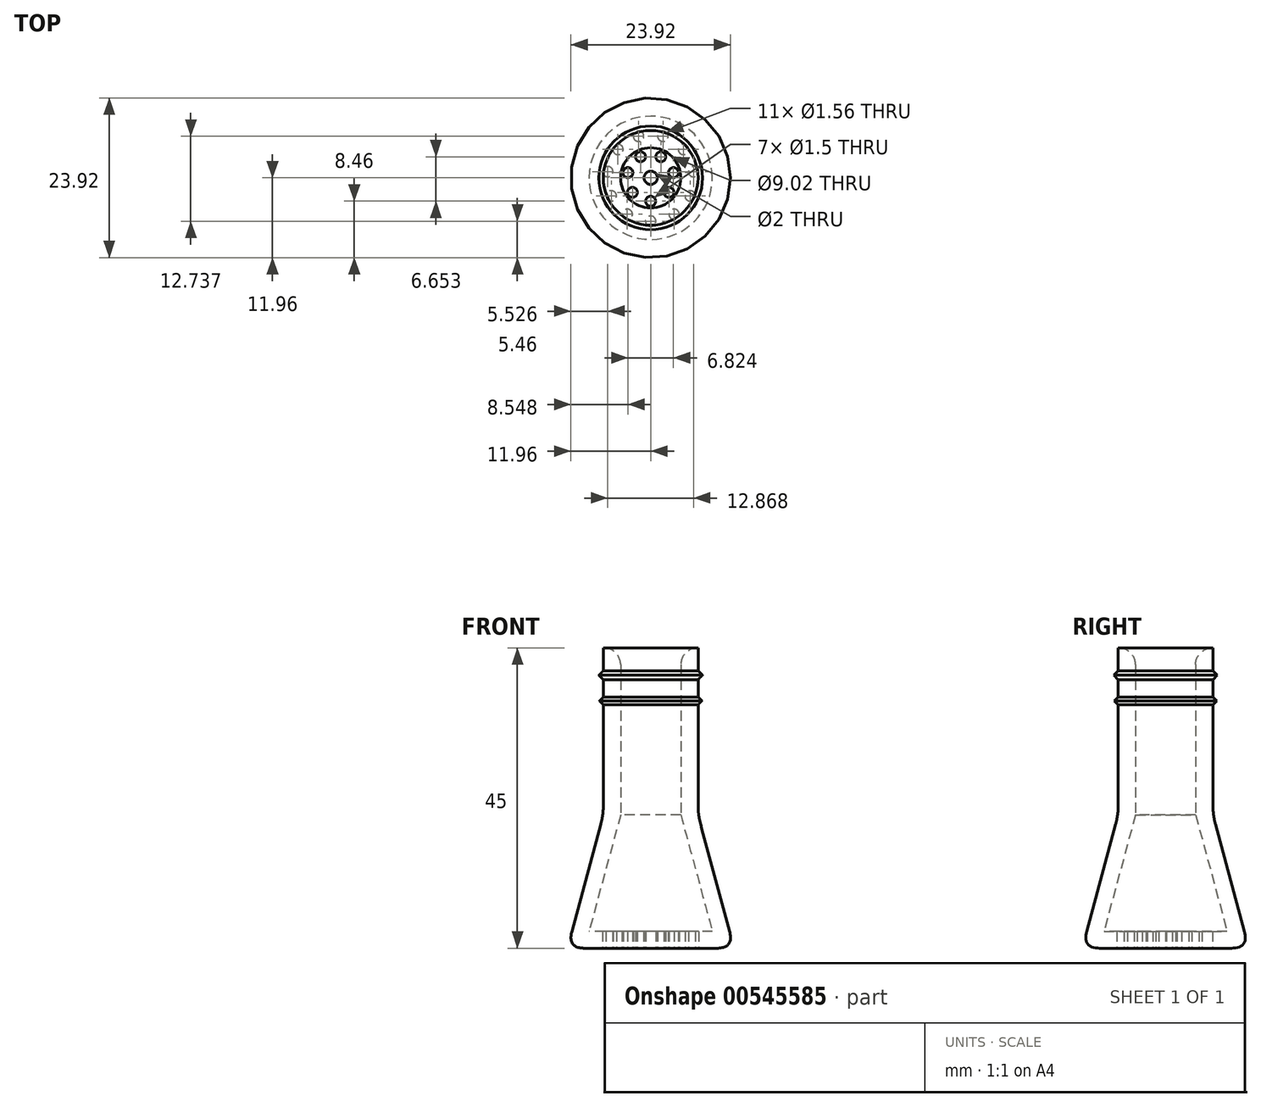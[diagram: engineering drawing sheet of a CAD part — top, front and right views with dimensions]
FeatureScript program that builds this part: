
annotation { "Feature Type Name" : "Feature", "Feature Type Description" : "" }
export const myFeature = defineFeature(function(context is Context, id is Id, definition is map)
    precondition{}
    {
        {
            var Q0;
            Q0=qCreatedBy(makeId("Top.planeOp"),FACE);
            var sketch = newSketch(context, id + "F0", { "sketchPlane" : qUnion([Q0])});
            skCircle(sketch, "E0", {"center": v(0, 0) * mm, "radius": 12.5 * mm});
            skSolve(sketch);
        }
        {
            var Q0;
            Q0=qCreatedBy(makeId("Top.planeOp"),FACE);
            cPlane(context, id + "F1", {"entities" : qUnion([Q0]), "cplaneType" : CPlaneType.OFFSET, "offset" : 20 * mm, "width" : 150 * mm, "height" : 150 * mm});
        }
        {
            var Q0;
            Q0=qCreatedBy(id+"F1.planeOp",FACE);
            var sketch = newSketch(context, id + "F2", { "sketchPlane" : qUnion([Q0])});
            skCircle(sketch, "E1", {"center": v(0, 0) * mm, "radius": 7.1 * mm});
            skSolve(sketch);
        }
        {
            var Q0;
            Q0=makeQuery(id+"F0.imprint","IMPRINT",FACE,{"disambiguationData":[TD([[makeQuery(id+"F0.imprint","IMPRINT",EDGE,{"derivedFrom":sQuery(id+"F0.wireOp",EDGE,"E0")}),1.0]])]});
            var Q1;
            Q1=makeQuery(id+"F2.imprint","IMPRINT",FACE,{"disambiguationData":[TD([[makeQuery(id+"F2.imprint","IMPRINT",EDGE,{"derivedFrom":sQuery(id+"F2.wireOp",EDGE,"E1")}),1.0]])]});
            loft(context, id + "F3", {"sheetProfilesArray" : [{ "sheetProfileEntities" : qUnion([Q0]) }, { "sheetProfileEntities" : qUnion([Q1]) }]});
        }
        {
            var Q0;
            Q0=makeQuery(id+"F3.opLoft","CAP_FACE",FACE,{"disambiguationData":[OSD([makeQuery(id+"F2.imprint","IMPRINT",FACE,{"disambiguationData":[TD([[makeQuery(id+"F2.imprint","IMPRINT",EDGE,{"derivedFrom":sQuery(id+"F2.wireOp",EDGE,"E1")}),1.0]])]})])],"isStart":true});
            var Q1;
            Q1=makeQuery(id+"F5.opExtrude","SWEPT_FACE",FACE,{"disambiguationData":[OSD([sQuery(id+"F0.wireOp",EDGE,"E0"),sQuery(id+"F2.wireOp",EDGE,"E1")])]});
            var Q2;
            Q2=makeQuery(id+"F3.opLoft","SWEPT_BODY",BODY,{"disambiguationData":[OSD([makeQuery(id+"F0.imprint","IMPRINT",FACE,{"disambiguationData":[TD([[makeQuery(id+"F0.imprint","IMPRINT",EDGE,{"derivedFrom":sQuery(id+"F0.wireOp",EDGE,"E0")}),1.0]])]}),makeQuery(id+"F2.imprint","IMPRINT",FACE,{"disambiguationData":[TD([[makeQuery(id+"F2.imprint","IMPRINT",EDGE,{"derivedFrom":sQuery(id+"F2.wireOp",EDGE,"E1")}),1.0]])]})])]});
            shell(context, id + "F4", {"entities" : qUnion([Q0, Q1]), "parts" : qUnion([Q2]), "thickness" : 2.5 * mm});
        }
        {
            var Q0;
            Q0=makeQuery(id+"F0ecNTMsgWaadGP_1.imprint","IMPRINT",FACE,{"disambiguationData":[TD([[makeQuery(id+"F0ecNTMsgWaadGP_1.imprint","IMPRINT",EDGE,{"derivedFrom":sQuery(id+"F0ecNTMsgWaadGP_1.wireOp",EDGE,"DrDFBUXE-mWmM-yVQ1-YrQf-KKvgjwECMo2q")}),1.0]])]});
            var Q1;
            Q1=makeQuery(id+"F3.opLoft","CAP_FACE",FACE,{"disambiguationData":[OSD([makeQuery(id+"F2.imprint","IMPRINT",FACE,{"disambiguationData":[TD([[makeQuery(id+"F2.imprint","IMPRINT",EDGE,{"derivedFrom":sQuery(id+"F2.wireOp",EDGE,"E1")}),1.0]])]})])],"isStart":true});
            extrude(context, id + "F5", {"entities" : qUnion([Q0, Q1]), "operationType" : NewBodyOperationType.ADD, "depth" : 25 * mm, "offsetDistance" : 25 * mm});
        }
        {
            var Q0;
            Q0=makeQuery(id+"F3.opLoft","CAP_FACE",FACE,{"disambiguationData":[OSD([makeQuery(id+"F0.imprint","IMPRINT",FACE,{"disambiguationData":[TD([[makeQuery(id+"F0.imprint","IMPRINT",EDGE,{"derivedFrom":sQuery(id+"F0.wireOp",EDGE,"E0")}),1.0]])]})])],"isStart":true});
            var sketch = newSketch(context, id + "F6", { "sketchPlane" : qUnion([Q0])});
            skCircle(sketch, "E2", {"center": v(0, 0) * mm, "radius": 1 * mm});
            skCircle(sketch, "E3", {"center": v(0, 3.5) * mm, "radius": 0.75 * mm});
            skCircle(sketch, "E4.1.0", {"center": v(-2.74, 2.18) * mm, "radius": 0.75 * mm});
            skCircle(sketch, "E4.2.0", {"center": v(-3.41, -0.78) * mm, "radius": 0.75 * mm});
            skCircle(sketch, "E4.3.0", {"center": v(-1.52, -3.15) * mm, "radius": 0.75 * mm});
            skCircle(sketch, "E4.4.0", {"center": v(1.52, -3.15) * mm, "radius": 0.75 * mm});
            skCircle(sketch, "E5.1.5.0", {"center": v(3.41, -0.78) * mm, "radius": 0.75 * mm});
            skCircle(sketch, "E5.1.6.0", {"center": v(2.74, 2.18) * mm, "radius": 0.75 * mm});
            skCircle(sketch, "E6", {"center": v(0, 6.5) * mm, "radius": 0.78 * mm});
            skCircle(sketch, "E7.1.0", {"center": v(-3.51, 5.47) * mm, "radius": 0.78 * mm});
            skCircle(sketch, "E7.2.0", {"center": v(-5.91, 2.7) * mm, "radius": 0.78 * mm});
            skCircle(sketch, "E7.3.0", {"center": v(-6.43, -0.93) * mm, "radius": 0.78 * mm});
            skCircle(sketch, "E7.4.0", {"center": v(-4.91, -4.26) * mm, "radius": 0.78 * mm});
            skCircle(sketch, "E7.5.0", {"center": v(-1.83, -6.24) * mm, "radius": 0.78 * mm});
            skCircle(sketch, "E7.6.0", {"center": v(1.83, -6.24) * mm, "radius": 0.78 * mm});
            skCircle(sketch, "E7.7.0", {"center": v(4.91, -4.26) * mm, "radius": 0.78 * mm});
            skCircle(sketch, "E7.8.0", {"center": v(6.43, -0.93) * mm, "radius": 0.78 * mm});
            skCircle(sketch, "E7.9.0", {"center": v(5.91, 2.7) * mm, "radius": 0.78 * mm});
            skCircle(sketch, "E8.0.10.0", {"center": v(3.51, 5.47) * mm, "radius": 0.78 * mm});
            skSolve(sketch);
        }
        {
            var Q0;
            Q0=makeQuery(id+"F3.opLoft","MID_CAP_EDGE",EDGE,{"disambiguationData":[OSD([sQuery(id+"F0.wireOp",EDGE,"E0")])],"capPos":0.0});
            fillet(context, id + "F7", {"entities" : qUnion([Q0]), "radius" : 2 * mm, "tangentPropagation" : true, "rho" : .5, "crossSection" : FilletCrossSection.CONIC, "allowEdgeOverflow" : false});
        }
        {
            var Q0;
            Q0=makeQuery(id+"F6.imprint","IMPRINT",FACE,{"disambiguationData":[TD([[makeQuery(id+"F6.imprint","IMPRINT",EDGE,{"derivedFrom":sQuery(id+"F6.wireOp",EDGE,"E4.1.0")}),1.0]])]});
            var Q1;
            Q1=makeQuery(id+"F6.imprint","IMPRINT",FACE,{"disambiguationData":[TD([[makeQuery(id+"F6.imprint","IMPRINT",EDGE,{"derivedFrom":sQuery(id+"F6.wireOp",EDGE,"E4.2.0")}),1.0]])]});
            var Q2;
            Q2=makeQuery(id+"F6.imprint","IMPRINT",FACE,{"disambiguationData":[TD([[makeQuery(id+"F6.imprint","IMPRINT",EDGE,{"derivedFrom":sQuery(id+"F6.wireOp",EDGE,"E2")}),1.0]])]});
            var Q3;
            Q3=makeQuery(id+"F6.imprint","IMPRINT",FACE,{"disambiguationData":[TD([[makeQuery(id+"F6.imprint","IMPRINT",EDGE,{"derivedFrom":sQuery(id+"F6.wireOp",EDGE,"E4.3.0")}),1.0]])]});
            var Q4;
            Q4=makeQuery(id+"F6.imprint","IMPRINT",FACE,{"disambiguationData":[TD([[makeQuery(id+"F6.imprint","IMPRINT",EDGE,{"derivedFrom":sQuery(id+"F6.wireOp",EDGE,"E4.4.0")}),1.0]])]});
            var Q5;
            Q5=makeQuery(id+"F6.imprint","IMPRINT",FACE,{"disambiguationData":[TD([[makeQuery(id+"F6.imprint","IMPRINT",EDGE,{"derivedFrom":sQuery(id+"F6.wireOp",EDGE,"E3")}),1.0]])]});
            var Q6;
            Q6=makeQuery(id+"F6.imprint","IMPRINT",FACE,{"disambiguationData":[TD([[makeQuery(id+"F6.imprint","IMPRINT",EDGE,{"derivedFrom":sQuery(id+"F6.wireOp",EDGE,"E5.1.6.0")}),1.0]])]});
            var Q7;
            Q7=makeQuery(id+"F6.imprint","IMPRINT",FACE,{"disambiguationData":[TD([[makeQuery(id+"F6.imprint","IMPRINT",EDGE,{"derivedFrom":sQuery(id+"F6.wireOp",EDGE,"E5.1.5.0")}),1.0]])]});
            var Q8;
            Q8=makeQuery(id+"F6.imprint","IMPRINT",FACE,{"disambiguationData":[TD([[makeQuery(id+"F6.imprint","IMPRINT",EDGE,{"derivedFrom":sQuery(id+"F6.wireOp",EDGE,"E8.0.10.0")}),1.0]])]});
            var Q9;
            Q9=makeQuery(id+"F6.imprint","IMPRINT",FACE,{"disambiguationData":[TD([[makeQuery(id+"F6.imprint","IMPRINT",EDGE,{"derivedFrom":sQuery(id+"F6.wireOp",EDGE,"E7.9.0")}),1.0]])]});
            var Q10;
            Q10=makeQuery(id+"F6.imprint","IMPRINT",FACE,{"disambiguationData":[TD([[makeQuery(id+"F6.imprint","IMPRINT",EDGE,{"derivedFrom":sQuery(id+"F6.wireOp",EDGE,"E7.8.0")}),1.0]])]});
            var Q11;
            Q11=makeQuery(id+"F6.imprint","IMPRINT",FACE,{"disambiguationData":[TD([[makeQuery(id+"F6.imprint","IMPRINT",EDGE,{"derivedFrom":sQuery(id+"F6.wireOp",EDGE,"E7.7.0")}),1.0]])]});
            var Q12;
            Q12=makeQuery(id+"F6.imprint","IMPRINT",FACE,{"disambiguationData":[TD([[makeQuery(id+"F6.imprint","IMPRINT",EDGE,{"derivedFrom":sQuery(id+"F6.wireOp",EDGE,"E7.6.0")}),1.0]])]});
            var Q13;
            Q13=makeQuery(id+"F6.imprint","IMPRINT",FACE,{"disambiguationData":[TD([[makeQuery(id+"F6.imprint","IMPRINT",EDGE,{"derivedFrom":sQuery(id+"F6.wireOp",EDGE,"E7.5.0")}),1.0]])]});
            var Q14;
            Q14=makeQuery(id+"F6.imprint","IMPRINT",FACE,{"disambiguationData":[TD([[makeQuery(id+"F6.imprint","IMPRINT",EDGE,{"derivedFrom":sQuery(id+"F6.wireOp",EDGE,"E7.4.0")}),1.0]])]});
            var Q15;
            Q15=makeQuery(id+"F6.imprint","IMPRINT",FACE,{"disambiguationData":[TD([[makeQuery(id+"F6.imprint","IMPRINT",EDGE,{"derivedFrom":sQuery(id+"F6.wireOp",EDGE,"E7.3.0")}),1.0]])]});
            var Q16;
            Q16=makeQuery(id+"F6.imprint","IMPRINT",FACE,{"disambiguationData":[TD([[makeQuery(id+"F6.imprint","IMPRINT",EDGE,{"derivedFrom":sQuery(id+"F6.wireOp",EDGE,"E7.2.0")}),1.0]])]});
            var Q17;
            Q17=makeQuery(id+"F6.imprint","IMPRINT",FACE,{"disambiguationData":[TD([[makeQuery(id+"F6.imprint","IMPRINT",EDGE,{"derivedFrom":sQuery(id+"F6.wireOp",EDGE,"E7.1.0")}),1.0]])]});
            var Q18;
            Q18=makeQuery(id+"F6.imprint","IMPRINT",FACE,{"disambiguationData":[TD([[makeQuery(id+"F6.imprint","IMPRINT",EDGE,{"derivedFrom":sQuery(id+"F6.wireOp",EDGE,"E6")}),1.0]])]});
            var Q19;
            Q19=makeQuery(id+"F3.opLoft","CAP_FACE",FACE,{"disambiguationData":[OSD([makeQuery(id+"F2.imprint","IMPRINT",FACE,{"disambiguationData":[TD([[makeQuery(id+"F2.imprint","IMPRINT",EDGE,{"derivedFrom":sQuery(id+"F2.wireOp",EDGE,"E1")}),1.0]])]})])],"isStart":true});
            extrude(context, id + "F8", {"entities" : qUnion([Q0, Q1, Q2, Q3, Q4, Q5, Q6, Q7, Q8, Q9, Q10, Q11, Q12, Q13, Q14, Q15, Q16, Q17, Q18]), "operationType" : NewBodyOperationType.REMOVE, "oppositeDirection" : true, "depth" : 3 * mm, "endBoundEntityFace" : qUnion([Q19]), "offsetDistance" : 25 * mm});
        }
        {
            var Q0;
            {var subQ0=sQuery(id+"F2.wireOp",EDGE,"E1");var subQ1=sQuery(id+"F0.wireOp",EDGE,"E0");var subQ2=makeQuery(id+"F3.opLoft","MID_CAP_EDGE",EDGE,{"disambiguationData":[OSD([subQ1,subQ0])],"capPos":1.0});Q0=makeQuery(id+"F5.boolean.opBoolean","MERGE",EDGE,{"derivedFrom":[subQ2,makeQuery(id+"F5.opExtrude","CAP_EDGE",EDGE,{"disambiguationData":[OSD([subQ1,subQ0]),TDD([subQ2])],"isStart":true})]});}
            fillet(context, id + "F9", {"entities" : qUnion([Q0]), "radius" : 11 * mm, "tangentPropagation" : true, "allowEdgeOverflow" : false});
        }
        {
            var Q0;
            Q0=qCreatedBy(makeId("Front.planeOp"),FACE);
            var sketch = newSketch(context, id + "F10", { "sketchPlane" : qUnion([Q0])});
            skLineSegment(sketch, "E9.bottom", {"start": v(6.68, 36.07) * mm, "end": v(7.68, 36.07) * mm});
            skLineSegment(sketch, "E9.top", {"start": v(6.68, 38.07) * mm, "end": v(7.68, 38.07) * mm});
            skLineSegment(sketch, "E9.left", {"start": v(6.68, 36.07) * mm, "end": v(6.68, 38.07) * mm});
            skLineSegment(sketch, "E9.right", {"start": v(7.68, 36.07) * mm, "end": v(7.68, 38.07) * mm});
            skLineSegment(sketch, "E10.bottom", {"start": v(6.77, 39.92) * mm, "end": v(7.77, 39.92) * mm});
            skLineSegment(sketch, "E10.top", {"start": v(6.77, 41.92) * mm, "end": v(7.77, 41.92) * mm});
            skLineSegment(sketch, "E10.left", {"start": v(6.77, 39.92) * mm, "end": v(6.77, 41.92) * mm});
            skLineSegment(sketch, "E10.right", {"start": v(7.77, 39.92) * mm, "end": v(7.77, 41.92) * mm});
            skSolve(sketch);
        }
        {
            var Q0;
            Q0=makeQuery(id+"F10.imprint","IMPRINT",FACE,{"disambiguationData":[TD([[makeQuery(id+"F10.imprint","IMPRINT",EDGE,{"derivedFrom":sQuery(id+"F10.wireOp",EDGE,"E9.bottom")}),1.0]])]});
            var Q1;
            Q1=makeQuery(id+"F10.imprint","IMPRINT",FACE,{"disambiguationData":[TD([[makeQuery(id+"F10.imprint","IMPRINT",EDGE,{"derivedFrom":sQuery(id+"F10.wireOp",EDGE,"E10.bottom")}),1.0]])]});
            var Q2;
            {var subQ0=sQuery(id+"F2.wireOp",EDGE,"E1");var subQ1=sQuery(id+"F0.wireOp",EDGE,"E0");Q2=makeQuery(id+"F5.opExtrude","SWEPT_FACE",FACE,{"disambiguationData":[OSD([subQ1,subQ0]),TDD([makeQuery(id+"F3.opLoft","MID_CAP_EDGE",EDGE,{"disambiguationData":[OSD([subQ1,subQ0])],"capPos":1.0})])]});}
            revolve(context, id + "F11", {"operationType" : NewBodyOperationType.ADD, "entities" : qUnion([Q0, Q1]), "axis" : qUnion([Q2]), "revolveType" : RevolveType.FULL});
        }
        {
            var Q0;
            Q0=makeQuery(id+"F11.opRevolve","SWEPT_EDGE",EDGE,{"disambiguationData":[OSD([sQuery(id+"F10.wireOp",EDGE,"E9.top"),sQuery(id+"F10.wireOp",EDGE,"E9.right")])]});
            var Q1;
            Q1=makeQuery(id+"F11.opRevolve","SWEPT_EDGE",EDGE,{"disambiguationData":[OSD([sQuery(id+"F10.wireOp",EDGE,"E9.bottom"),sQuery(id+"F10.wireOp",EDGE,"E9.right")])]});
            var Q2;
            Q2=makeQuery(id+"F11.opRevolve","SWEPT_EDGE",EDGE,{"disambiguationData":[OSD([sQuery(id+"F10.wireOp",EDGE,"E10.bottom"),sQuery(id+"F10.wireOp",EDGE,"E10.right")])]});
            var Q3;
            Q3=makeQuery(id+"F11.opRevolve","SWEPT_EDGE",EDGE,{"disambiguationData":[OSD([sQuery(id+"F10.wireOp",EDGE,"E10.top"),sQuery(id+"F10.wireOp",EDGE,"E10.right")])]});
            chamfer(context, id + "F12", {"entities" : qUnion([Q0, Q1, Q2, Q3]), "width" : 1 * mm, "tangentPropagation" : true});
        }
        {
            var Q0;
            {var subQ0=sQuery(id+"F2.wireOp",EDGE,"E1");var subQ1=sQuery(id+"F0.wireOp",EDGE,"E0");Q0=makeQuery(id+"F5.opExtrude","CAP_EDGE",EDGE,{"disambiguationData":[OSD([subQ1,subQ0]),TDD([makeQuery(id+"F4.opShell","OFFSET_EDGE",EDGE,{"disambiguationData":[OSD([subQ1,subQ0])]})])],"isStart":false});}
            fillet(context, id + "F13", {"entities" : qUnion([Q0]), "radius" : 2.5 * mm, "tangentPropagation" : true, "allowEdgeOverflow" : false});
        }
    });
